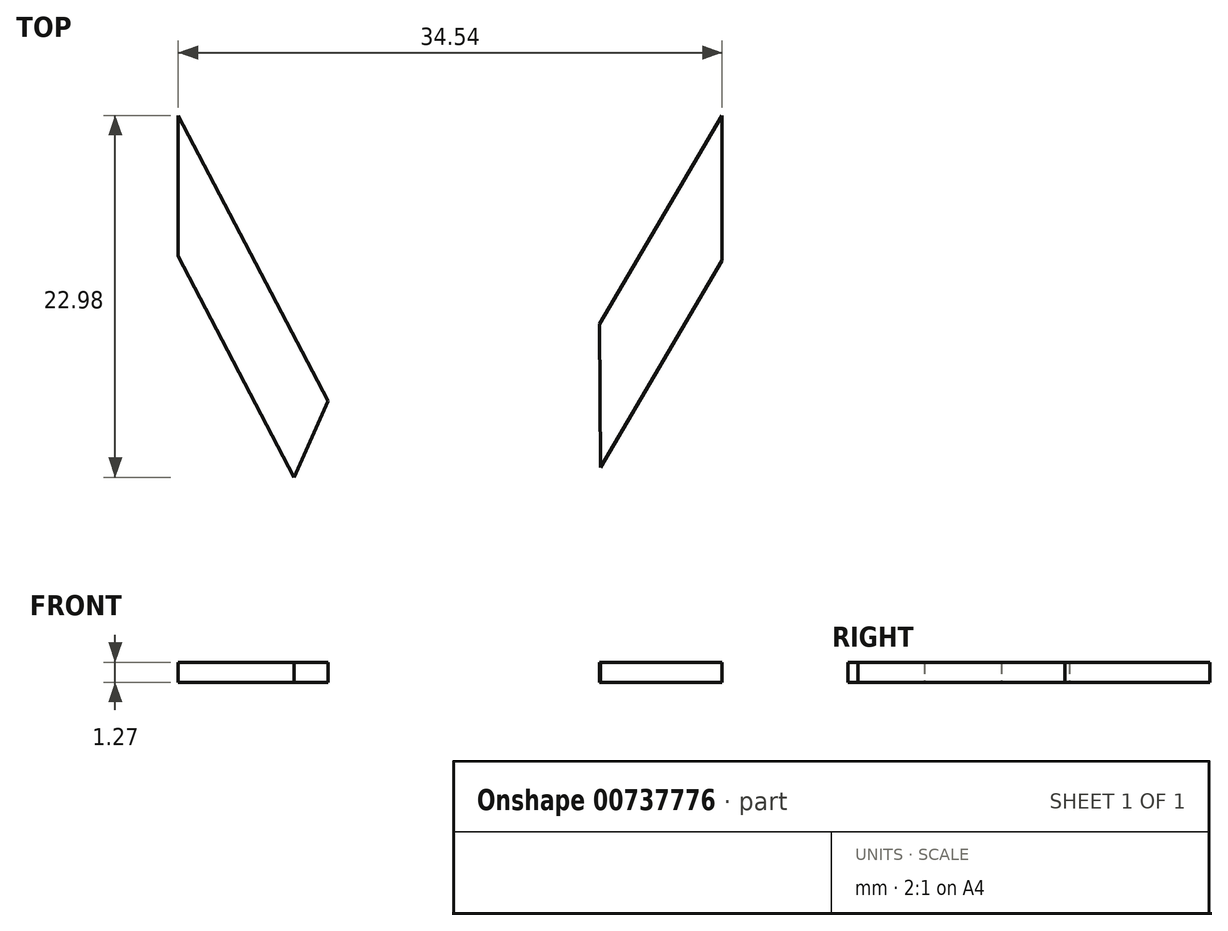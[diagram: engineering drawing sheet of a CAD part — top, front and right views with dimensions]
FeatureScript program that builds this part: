
annotation { "Feature Type Name" : "Feature", "Feature Type Description" : "" }
export const myFeature = defineFeature(function(context is Context, id is Id, definition is map)
    precondition{}
    {
        {
            var Q0;
            Q0=qCreatedBy(makeId("Top.planeOp"),FACE);
            var sketch = newSketch(context, id + "F0", { "sketchPlane" : qUnion([Q0])});
            skLineSegment(sketch, "E0", {"start": v(-21.15, 8.78) * mm, "end": v(-30.65, 26.9) * mm});
            skLineSegment(sketch, "E1", {"start": v(-30.65, 26.9) * mm, "end": v(-30.65, 17.99) * mm});
            skLineSegment(sketch, "E2", {"start": v(-30.65, 17.99) * mm, "end": v(-23.29, 3.93) * mm});
            skLineSegment(sketch, "E3", {"start": v(-23.29, 3.93) * mm, "end": v(-21.15, 8.78) * mm});
            skLineSegment(sketch, "E4", {"start": v(-3.89, 13.67) * mm, "end": v(3.89, 26.9) * mm});
            skLineSegment(sketch, "E5", {"start": v(3.89, 26.9) * mm, "end": v(3.89, 17.7) * mm});
            skLineSegment(sketch, "E6", {"start": v(3.89, 17.7) * mm, "end": v(-3.82, 4.56) * mm});
            skLineSegment(sketch, "E7", {"start": v(-3.82, 4.56) * mm, "end": v(-3.89, 13.67) * mm});
            skSolve(sketch);
        }
        {
            var Q0;
            Q0 = qSketchRegion(id + "F0", true);
            extrude(context, id + "F1", {"entities" : qUnion([Q0]), "depth" : 1.27 * mm, "offsetDistance" : 25.4 * mm});
        }
    });
